# Revit family: Haworth_Planes_ConferenceTable_HexagonThreePiece
name_source: partatom
category: Furniture Systems
revit_build: Autodesk Revit 2018 (Build: 20170223_1515(x64)
units: mm (PartAtom-declared; Revit-internal decimal feet)

## family parameters
Always vertical = Yes
Cut with Voids When Loaded = No
OmniClass Number = 23.40.70.14.64.21
OmniClass Title = Systems Furniture
Part Type = Normal
Room Calculation Point = No
Round Connector Dimension = Use Diameter
Shared = No
Work Plane-Based = No

## types (1)
- 270w 60d
    Actual Depth = 60"
    Actual Height = 29"
    Actual Width = 270"
    Assembly Code = E2020200
    Cable Base = Yes
    Center Leg Control = No
    Custom Size = No
    Cutout = Yes
    Cutout Depth = 4"
    Cutout Side Offset = 22 1/2"
    Cutout Width = 8"
    Depth = 60"
    Description = Haworth - Planes Conference Table - Hexagon Three Piece - 270w 60d
    Edgeband = Yes
    Flip Top = Yes
    Flip Top Finish = Haworth _ Paint _ Metallic Champagne
    Fliptop Center Vis. = Yes
    Fliptop Depth = 4 3/8"
    Fliptop Side Vis. = No
    Fliptop Width = 8 1/4"
    Knife Edge = No
    Manufacturer = Haworth
    Max. Depth = 60"
    Max. Height = 29"
    Max. Width = 270"
    Middle Leg Control = Yes
    Min. Depth = 42"
    Min. Height = 29"
    Min. Width = 186"
    Min/Max Width = 186-270 @ 6 in. increments
    Model = TARX
    Not Cable Base = No
    Opening Center = Yes
    Opening Double = No
    Opening Double Wide = No
    Opening Left/Right = No
    Opening Single = Yes
    Opening Single Wide = No
    Revision Number = 1
    Side Middle Leg Control = Yes
    Standard Depths = 42, 48, 54, 60 in.
    Standard Height = 29 in.
    Support Height = 27 13/16"
    Support Location FrontBack = 8 3/4"
    Support Location Side = 10"
    Sustainability Info = https://www.haworth.com
    Table Thickness = 1 3/16"
    Third Width = 45"
    URL = www.haworth.com
    URL - Product = http://www.haworth.com
    Warranty = http://www.haworth.com
    Width = 270"

## geometry (parser evidence)
native form markers: Sweep x7
no freeform markers — native parametric forms only
